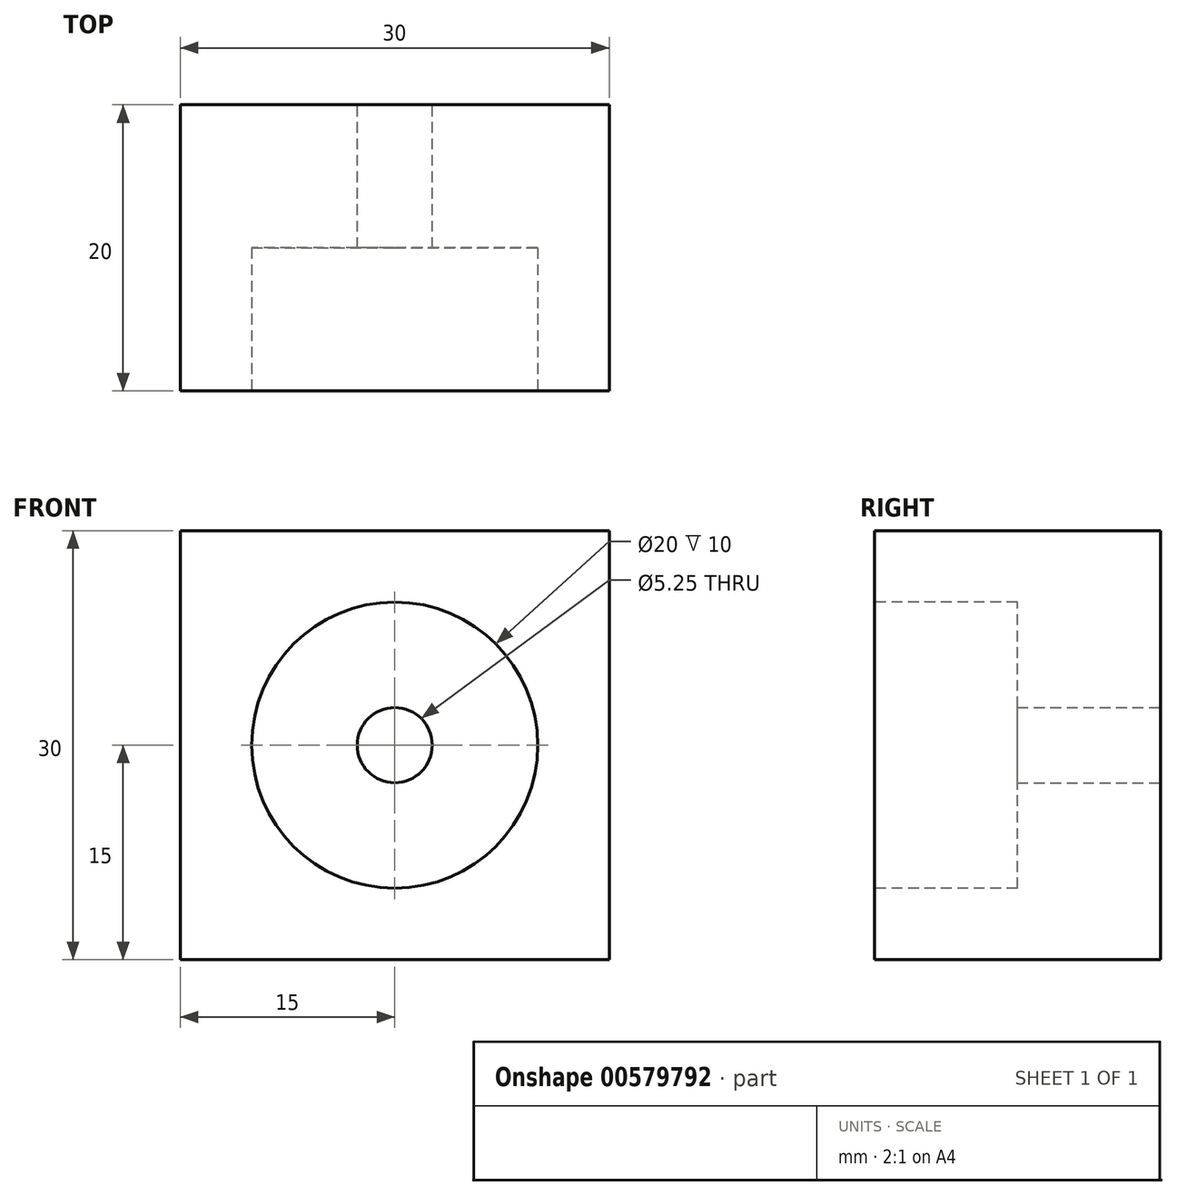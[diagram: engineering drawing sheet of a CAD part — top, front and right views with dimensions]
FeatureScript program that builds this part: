
annotation { "Feature Type Name" : "Feature", "Feature Type Description" : "" }
export const myFeature = defineFeature(function(context is Context, id is Id, definition is map)
    precondition{}
    {
        {
            var Q0;
            Q0=qCreatedBy(makeId("Front.planeOp"),FACE);
            var sketch = newSketch(context, id + "F0", { "sketchPlane" : qUnion([Q0])});
            skLineSegment(sketch, "E0.bottom", {"start": v(15, 15) * mm, "end": v(-15, 15) * mm});
            skLineSegment(sketch, "E0.top", {"start": v(15, -15) * mm, "end": v(-15, -15) * mm});
            skLineSegment(sketch, "E0.left", {"start": v(15, 15) * mm, "end": v(15, -15) * mm});
            skLineSegment(sketch, "E0.right", {"start": v(-15, 15) * mm, "end": v(-15, -15) * mm});
            skPoint(sketch, "E0.middle", {"position": v(0, 0) * mm});
            skSolve(sketch);
        }
        {
            var Q0;
            Q0=makeQuery(id+"F0.imprint","IMPRINT",FACE,{"disambiguationData":[TD([[makeQuery(id+"F0.imprint","IMPRINT",EDGE,{"derivedFrom":sQuery(id+"F0.wireOp",EDGE,"E0.bottom")}),1.0]])]});
            extrude(context, id + "F1", {"entities" : qUnion([Q0]), "endBound" : BoundingType.SYMMETRIC, "depth" : 20 * mm, "offsetDistance" : 25.4 * mm});
        }
        {
            var Q0;
            Q0=makeQuery(id+"F1.opExtrude","CAP_FACE",FACE,{"disambiguationData":[OSD([sQuery(id+"F0.wireOp",EDGE,"E0.bottom"),sQuery(id+"F0.wireOp",EDGE,"E0.top"),sQuery(id+"F0.wireOp",EDGE,"E0.left"),sQuery(id+"F0.wireOp",EDGE,"E0.right")])],"isStart":false});
            var sketch = newSketch(context, id + "F2", { "sketchPlane" : qUnion([Q0])});
            skCircle(sketch, "E1", {"center": v(0, 0) * mm, "radius": 10 * mm});
            skSolve(sketch);
        }
        {
            var Q0;
            Q0=makeQuery(id+"F2.imprint","IMPRINT",FACE,{"disambiguationData":[TD([[makeQuery(id+"F2.imprint","IMPRINT",EDGE,{"derivedFrom":sQuery(id+"F2.wireOp",EDGE,"E1")}),1.0]])]});
            extrude(context, id + "F3", {"entities" : qUnion([Q0]), "operationType" : NewBodyOperationType.REMOVE, "oppositeDirection" : true, "depth" : 10 * mm, "offsetDistance" : 25.4 * mm});
        }
        {
            var Q0;
            Q0=makeQuery(id+"F1.opExtrude","CAP_FACE",FACE,{"disambiguationData":[OSD([sQuery(id+"F0.wireOp",EDGE,"E0.bottom"),sQuery(id+"F0.wireOp",EDGE,"E0.top"),sQuery(id+"F0.wireOp",EDGE,"E0.left"),sQuery(id+"F0.wireOp",EDGE,"E0.right")])],"isStart":true});
            var sketch = newSketch(context, id + "F4", { "sketchPlane" : qUnion([Q0])});
            skPoint(sketch, "E2", {"position": v(0, 0) * mm});
            skSolve(sketch);
        }
        {
            var Q0;
            Q0=sQuery(id+"F4.wireOp",VERTEX,"E2");
            var Q1;
            Q1=makeQuery(id+"F1.opExtrude","SWEPT_BODY",BODY,{"disambiguationData":[OSD([sQuery(id+"F0.wireOp",EDGE,"E0.bottom"),sQuery(id+"F0.wireOp",EDGE,"E0.top"),sQuery(id+"F0.wireOp",EDGE,"E0.left"),sQuery(id+"F0.wireOp",EDGE,"E0.right")])]});
            hole(context, id + "F5", {"style" : HoleStyle.SIMPLE, "endStyle" : HoleEndStyle.THROUGH, "standardTappedOrClearance" : lookupTablePath({ "standard" : "ISO", "fit" : "Close", "size" : "M5", "type" : "Clearance" }), "standardBlindInLast" : lookupTablePath({ "fit" : "Close", "standard" : "ISO", "size" : "M5", "type" : "Clearance" }), "holeDiameter" : 5.25 * mm, "isTappedThrough" : true, "tappedDepth" : 12.7 * mm, "tapClearance" : 3, "locations" : qUnion([Q0]), "scope" : qUnion([Q1])});
        }
    });
